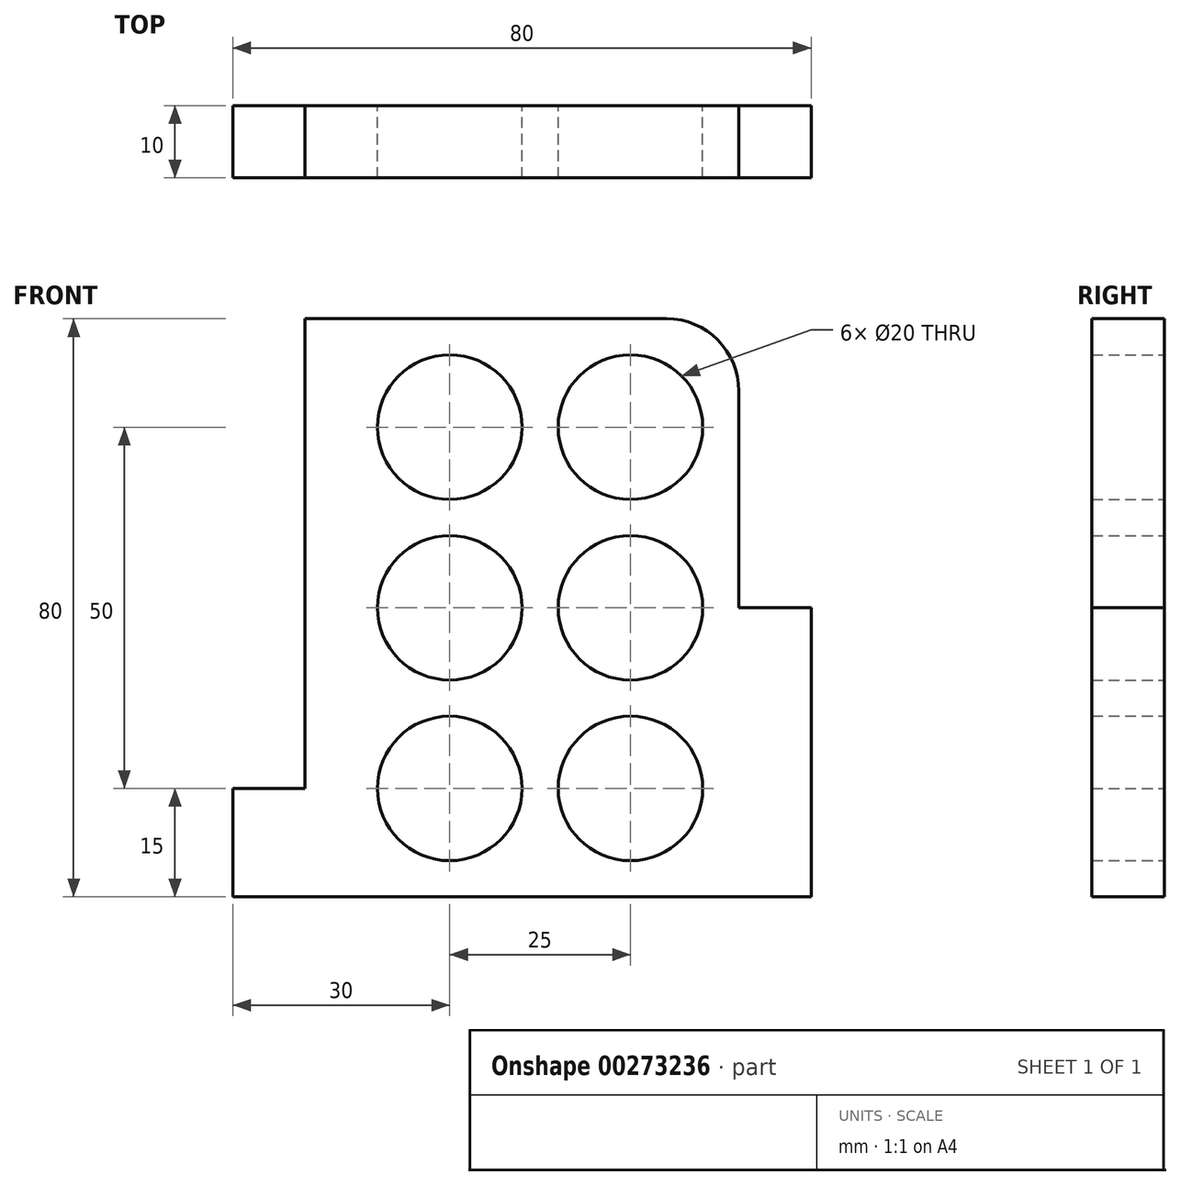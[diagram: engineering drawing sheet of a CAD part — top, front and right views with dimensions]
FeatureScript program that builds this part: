
annotation { "Feature Type Name" : "Feature", "Feature Type Description" : "" }
export const myFeature = defineFeature(function(context is Context, id is Id, definition is map)
    precondition{}
    {
        {
            var Q0;
            Q0=qCreatedBy(makeId("Front.planeOp"),FACE);
            var sketch = newSketch(context, id + "F0", { "sketchPlane" : qUnion([Q0])});
            skLineSegment(sketch, "E0", {"start": v(0, 0) * mm, "end": v(0, 15) * mm});
            skLineSegment(sketch, "E1", {"start": v(0, 15) * mm, "end": v(10, 15) * mm});
            skLineSegment(sketch, "E2", {"start": v(10, 15) * mm, "end": v(10, 80) * mm});
            skLineSegment(sketch, "E3", {"start": v(0, 0) * mm, "end": v(80, 0) * mm});
            skLineSegment(sketch, "E4", {"start": v(80, 0) * mm, "end": v(80, 40) * mm});
            skLineSegment(sketch, "E5", {"start": v(80, 40) * mm, "end": v(70, 40) * mm});
            skLineSegment(sketch, "E6", {"start": v(70, 40) * mm, "end": v(70, 70) * mm});
            skLineSegment(sketch, "E7", {"start": v(10, 80) * mm, "end": v(60, 80) * mm});
            skArc(sketch, "E8", {"start": v(70, 70) * mm, "mid": v(67.07, 77.07) * mm, "end": v(60, 80) * mm});
            skCircle(sketch, "E9", {"center": v(30, 65) * mm, "radius": 10 * mm});
            skCircle(sketch, "E10", {"center": v(55, 65) * mm, "radius": 10 * mm});
            skCircle(sketch, "E11", {"center": v(30, 40) * mm, "radius": 10 * mm});
            skCircle(sketch, "E12", {"center": v(55, 40) * mm, "radius": 10 * mm});
            skCircle(sketch, "E13", {"center": v(30, 15) * mm, "radius": 10 * mm});
            skCircle(sketch, "E14", {"center": v(55, 15) * mm, "radius": 10 * mm});
            skSolve(sketch);
        }
        {
            var Q0;
            Q0=makeQuery(id+"F0.imprint","IMPRINT",FACE,{"disambiguationData":[TD([[makeQuery(id+"F0.imprint","IMPRINT",EDGE,{"derivedFrom":sQuery(id+"F0.wireOp",EDGE,"E0")}),-1.0]])]});
            extrude(context, id + "F1", {"entities" : qUnion([Q0]), "depth" : 10 * mm});
        }
    });
